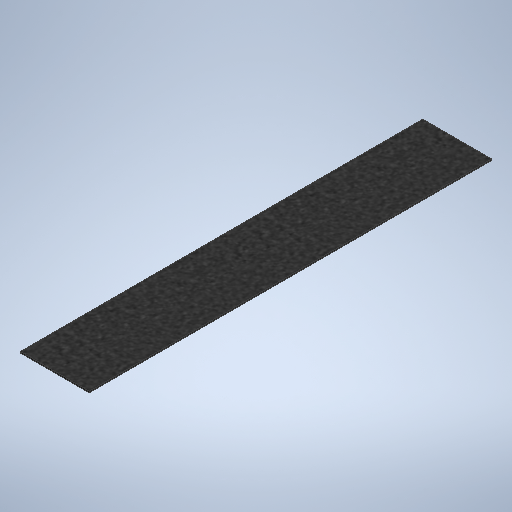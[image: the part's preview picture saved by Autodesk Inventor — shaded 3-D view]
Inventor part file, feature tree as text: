
AUTODESK INVENTOR PART (.ipt)
format: ipt  version: 2025.1 (Build 291241020, 241B)  size: 272,384 bytes
history: native  units: in
note: dims shown in document units (in); Inventor stores cm internally (conversion verified against a paired STEP export)
features: extrude x1, sketch x1
ambient origin geometry x8: Origin, YZ Plane, XZ Plane, XY Plane, X Axis, Y Axis, Z Axis, Center Point
bodies: Solid1 (feature_tree)
feature tree (2):
  extrude  "Extrusion1"  Depth=38.0in
  sketch  "Sketch1"  dims[d0=6.5in d1=38.0in d2=0.125in d3=0.0in]
